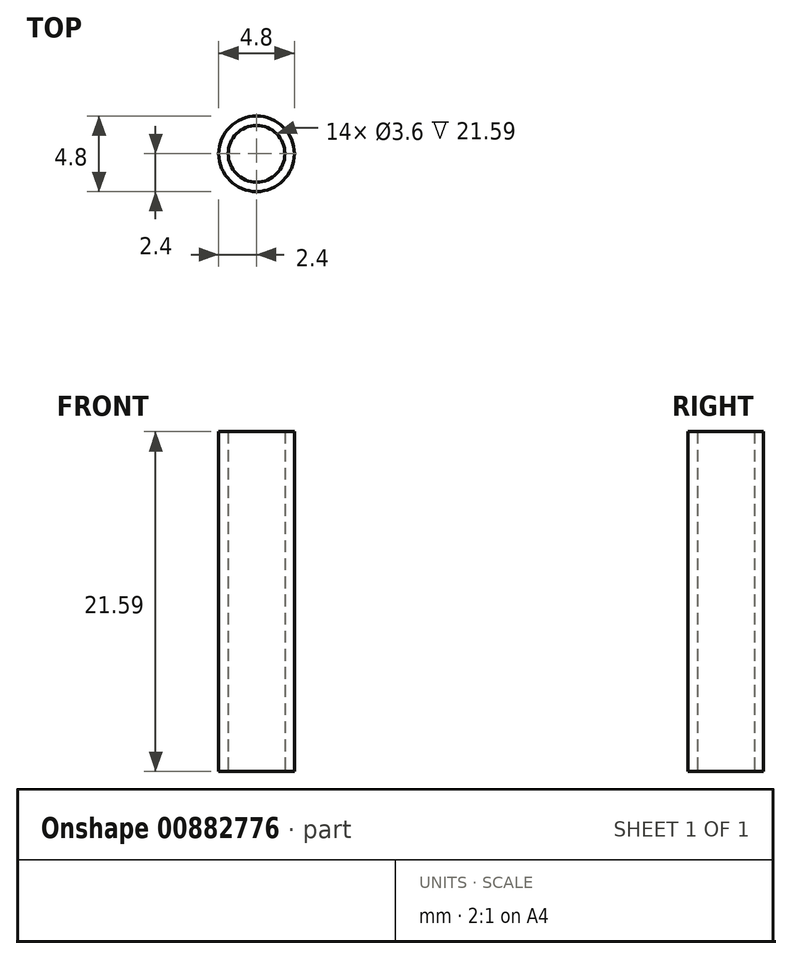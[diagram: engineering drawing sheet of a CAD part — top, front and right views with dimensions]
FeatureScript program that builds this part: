
annotation { "Feature Type Name" : "Feature", "Feature Type Description" : "" }
export const myFeature = defineFeature(function(context is Context, id is Id, definition is map)
    precondition{}
    {
        {
            var Q0;
            Q0=qCreatedBy(makeId("Top.planeOp"),FACE);
            var sketch = newSketch(context, id + "F0", { "sketchPlane" : qUnion([Q0])});
            skCircle(sketch, "E0", {"center": v(0, 0) * mm, "radius": 2.4 * mm});
            skCircle(sketch, "E1", {"center": v(0, 0) * mm, "radius": 1.8 * mm});
            skSolve(sketch);
        }
        {
            var Q0;
            Q0 = qSketchRegion(id + "F0", true);
            extrude(context, id + "F1", {"entities" : qUnion([Q0]), "depth" : 21.59 * mm, "offsetDistance" : 25.4 * mm});
        }
    });
